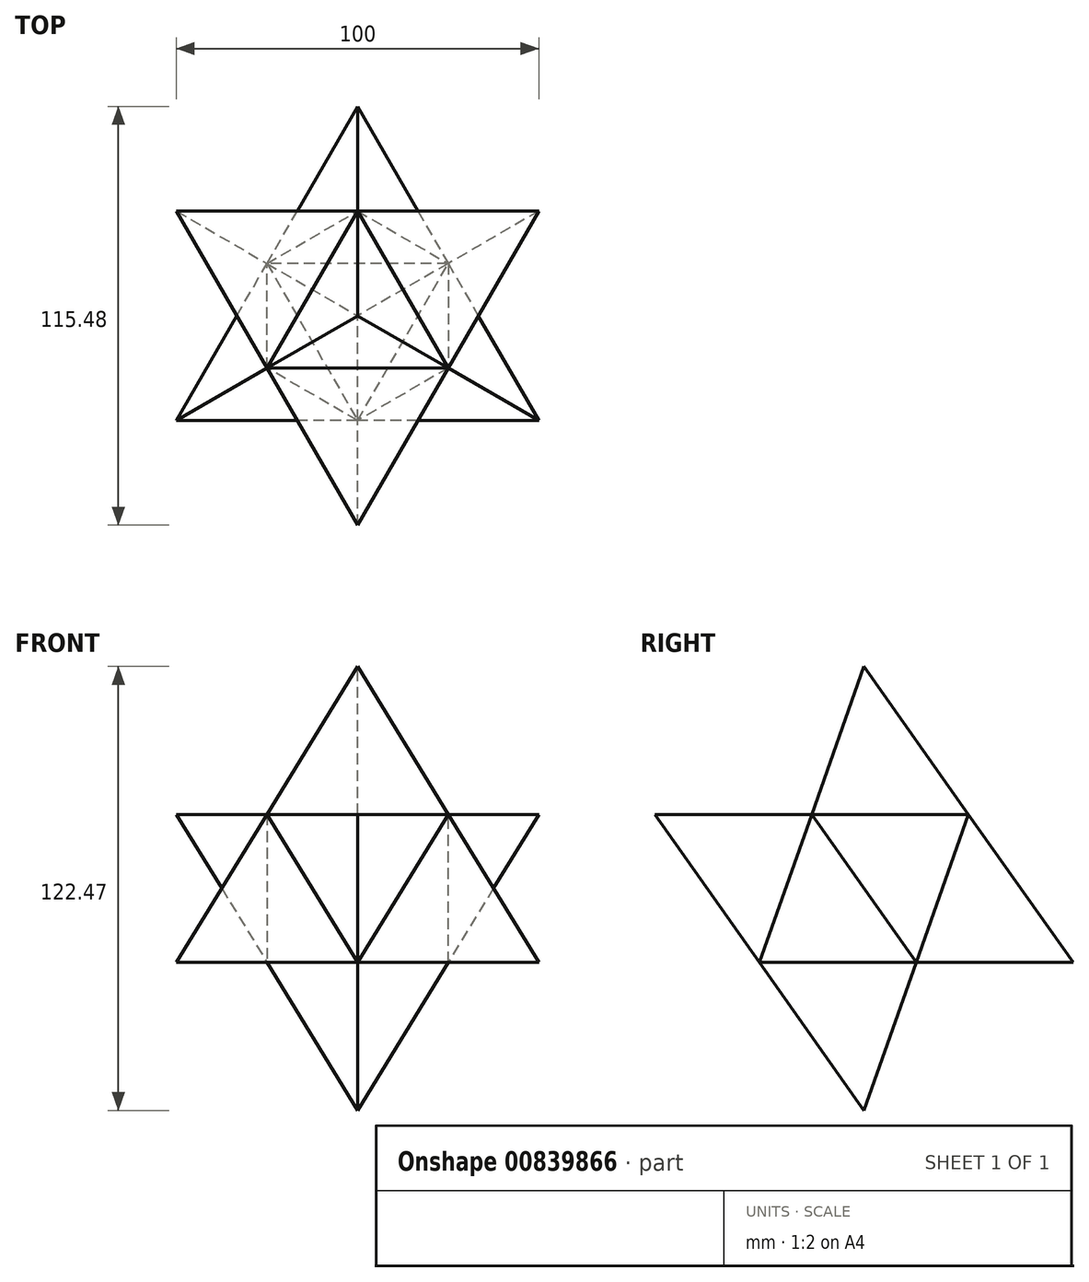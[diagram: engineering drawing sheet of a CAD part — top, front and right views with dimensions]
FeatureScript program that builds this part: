
annotation { "Feature Type Name" : "Feature", "Feature Type Description" : "" }
export const myFeature = defineFeature(function(context is Context, id is Id, definition is map)
    precondition{}
    {
        {
            var Q0;
            Q0=qCreatedBy(makeId("Top.planeOp"),FACE);
            var sketch = newSketch(context, id + "F0", { "sketchPlane" : qUnion([Q0])});
            skCircle(sketch, "E0.cCircle", {"center": v(0, 0) * mm, "radius": 28.87 * mm, "construction": true});
            skLineSegment(sketch, "E0.0", {"start": v(-50, -28.87) * mm, "end": v(0, 57.74) * mm});
            skLineSegment(sketch, "E0.1", {"start": v(0, 57.74) * mm, "end": v(50, -28.87) * mm});
            skLineSegment(sketch, "E0.2", {"start": v(50, -28.87) * mm, "end": v(-50, -28.87) * mm});
            skPoint(sketch, "E0.0.midPoint", {"position": v(-25, 14.43) * mm});
            skLineSegment(sketch, "E1", {"start": v(0, 57.74) * mm, "end": v(0, -28.87) * mm, "construction": true});
            skSolve(sketch);
        }
        {
            var Q0;
            Q0=qCreatedBy(makeId("Right.planeOp"),FACE);
            var sketch = newSketch(context, id + "F1", { "sketchPlane" : qUnion([Q0])});
            skLineSegment(sketch, "E2", {"start": v(0, 0) * mm, "end": v(0, 81.65) * mm, "construction": true});
            skLineSegment(sketch, "E3", {"start": v(0, 81.65) * mm, "end": v(-28.87, 0) * mm, "construction": true});
            skSolve(sketch);
        }
        {
            var Q0;
            Q0=makeQuery(id+"F0.imprint","IMPRINT",FACE,{"disambiguationData":[TD([[makeQuery(id+"F0.imprint","IMPRINT",EDGE,{"derivedFrom":sQuery(id+"F0.wireOp",EDGE,"E0.0")}),-1.0]])]});
            var Q1;
            Q1=sQuery(id+"F1.wireOp",VERTEX,"E2.end");
            loft(context, id + "F2", {"sheetProfilesArray" : [{ "sheetProfileEntities" : qUnion([Q0]) }, { "sheetProfileEntities" : qUnion([Q1]) }]});
        }
        {
            var Q0;
            {var subQ0=sQuery(id+"F0.wireOp",EDGE,"E0.2");var subQ1=sQuery(id+"F0.wireOp",EDGE,"E0.1");var subQ2=sQuery(id+"F0.wireOp",EDGE,"E0.0");Q0=makeQuery(id+"F2.opLoft","SWEPT_FACE",FACE,{"disambiguationData":[OSD([subQ2,subQ1,subQ0]),TDD([makeQuery(id+"F0.imprint","INTERSECT",VERTEX,{"derivedFrom":[subQ2,subQ0]}),makeQuery(id+"F0.imprint","INTERSECT",VERTEX,{"derivedFrom":[subQ1,subQ0]}),makeQuery(id+"F0.imprint","IMPRINT",EDGE,{"derivedFrom":subQ0})])]});}
            var sketch = newSketch(context, id + "F3", { "sketchPlane" : qUnion([Q0])});
            skLineSegment(sketch, "E4.0", {"start": v(41.34, -4.62) * mm, "end": v(0, 66.98) * mm});
            skLineSegment(sketch, "E4.1", {"start": v(-41.34, -4.62) * mm, "end": v(41.34, -4.62) * mm});
            skLineSegment(sketch, "E4.2", {"start": v(0, 66.98) * mm, "end": v(-41.34, -4.62) * mm});
            skSolve(sketch);
        }
        {
            var Q0;
            {var subQ0=sQuery(id+"F0.wireOp",EDGE,"E0.1");var subQ1=sQuery(id+"F0.wireOp",EDGE,"E0.2");var subQ2=sQuery(id+"F0.wireOp",EDGE,"E0.0");Q0=makeQuery(id+"F2.opLoft","SWEPT_FACE",FACE,{"disambiguationData":[OSD([subQ2,subQ0,subQ1]),TDD([makeQuery(id+"F0.imprint","INTERSECT",VERTEX,{"derivedFrom":[subQ2,subQ0]}),makeQuery(id+"F0.imprint","INTERSECT",VERTEX,{"derivedFrom":[subQ0,subQ1]}),makeQuery(id+"F0.imprint","IMPRINT",EDGE,{"derivedFrom":subQ0})])]});}
            var sketch = newSketch(context, id + "F4", { "sketchPlane" : qUnion([Q0])});
            skLineSegment(sketch, "E5.0", {"start": v(41.47, 3.27) * mm, "end": v(-12.66, 65.77) * mm});
            skLineSegment(sketch, "E5.1", {"start": v(-39.72, -12.35) * mm, "end": v(41.47, 3.27) * mm});
            skLineSegment(sketch, "E5.2", {"start": v(-12.66, 65.77) * mm, "end": v(-39.72, -12.35) * mm});
            skSolve(sketch);
        }
        {
            var Q0;
            {var subQ0=sQuery(id+"F0.wireOp",EDGE,"E0.0");var subQ1=sQuery(id+"F0.wireOp",EDGE,"E0.1");var subQ2=sQuery(id+"F0.wireOp",EDGE,"E0.2");Q0=makeQuery(id+"F2.opLoft","SWEPT_FACE",FACE,{"disambiguationData":[OSD([subQ0,subQ1,subQ2]),TDD([makeQuery(id+"F0.imprint","INTERSECT",VERTEX,{"derivedFrom":[subQ0,subQ2]}),makeQuery(id+"F0.imprint","INTERSECT",VERTEX,{"derivedFrom":[subQ0,subQ1]}),makeQuery(id+"F0.imprint","IMPRINT",EDGE,{"derivedFrom":subQ0})])]});}
            var sketch = newSketch(context, id + "F5", { "sketchPlane" : qUnion([Q0])});
            skLineSegment(sketch, "E6.0", {"start": v(39.72, -12.35) * mm, "end": v(12.66, 65.77) * mm});
            skLineSegment(sketch, "E6.1", {"start": v(-41.47, 3.27) * mm, "end": v(39.72, -12.35) * mm});
            skLineSegment(sketch, "E6.2", {"start": v(12.66, 65.77) * mm, "end": v(-41.47, 3.27) * mm});
            skSolve(sketch);
        }
        {
            var Q0;
            Q0=makeQuery(id+"F2.opLoft","CAP_FACE",FACE,{"disambiguationData":[OSD([makeQuery(id+"F0.imprint","IMPRINT",FACE,{"disambiguationData":[TD([[makeQuery(id+"F0.imprint","IMPRINT",EDGE,{"derivedFrom":sQuery(id+"F0.wireOp",EDGE,"E0.0")}),-1.0]])]})])],"isStart":true});
            var sketch = newSketch(context, id + "F6", { "sketchPlane" : qUnion([Q0])});
            skLineSegment(sketch, "E7.0", {"start": v(-41.34, 23.87) * mm, "end": v(41.34, 23.87) * mm});
            skLineSegment(sketch, "E7.1", {"start": v(0, -47.74) * mm, "end": v(-41.34, 23.87) * mm});
            skLineSegment(sketch, "E7.2", {"start": v(41.34, 23.87) * mm, "end": v(0, -47.74) * mm});
            skSolve(sketch);
        }
        {
            var Q0;
            Q0=makeQuery(id+"F2.opLoft","SWEPT_BODY",BODY,{"disambiguationData":[OSD([makeQuery(id+"F0.imprint","IMPRINT",FACE,{"disambiguationData":[TD([[makeQuery(id+"F0.imprint","IMPRINT",EDGE,{"derivedFrom":sQuery(id+"F0.wireOp",EDGE,"E0.0")}),-1.0]])]}),sQuery(id+"F1.wireOp",VERTEX,"E2.end")])]});
            var Q1;
            Q1=qCreatedBy(makeId("Top.planeOp"),FACE);
            mirror(context, id + "F7", {"entities" : qUnion([Q0]), "mirrorPlane" : qUnion([Q1])});
        }
        {
            var Q0;
            Q0=makeQuery(id+"F7.opPattern","COPY",BODY,{"derivedFrom":makeQuery(id+"F2.opLoft","SWEPT_BODY",BODY,{"disambiguationData":[OSD([makeQuery(id+"F0.imprint","IMPRINT",FACE,{"disambiguationData":[TD([[makeQuery(id+"F0.imprint","IMPRINT",EDGE,{"derivedFrom":sQuery(id+"F0.wireOp",EDGE,"E0.0")}),-1.0]])]}),sQuery(id+"F1.wireOp",VERTEX,"E2.end")])]}),"instanceName":"1"});
            var Q1;
            Q1=sQuery(id+"F1.wireOp",EDGE,"E2");
            transform(context, id + "F8", {"entities" : qUnion([Q0]), "transformType" : TransformType.ROTATION, "transformAxis" : qUnion([Q1]), "angle" : 60 * degree, "makeCopy" : false});
        }
        {
            var Q0;
            Q0=qCreatedBy(makeId("Front.planeOp"),FACE);
            var sketch = newSketch(context, id + "F9", { "sketchPlane" : qUnion([Q0])});
            skLineSegment(sketch, "E8", {"start": v(0, 0) * mm, "end": v(0, 40.82) * mm});
            skSolve(sketch);
        }
        {
            var Q0;
            Q0=makeQuery(id+"F7.opPattern","COPY",BODY,{"derivedFrom":makeQuery(id+"F2.opLoft","SWEPT_BODY",BODY,{"disambiguationData":[OSD([makeQuery(id+"F0.imprint","IMPRINT",FACE,{"disambiguationData":[TD([[makeQuery(id+"F0.imprint","IMPRINT",EDGE,{"derivedFrom":sQuery(id+"F0.wireOp",EDGE,"E0.0")}),-1.0]])]}),sQuery(id+"F1.wireOp",VERTEX,"E2.end")])]}),"instanceName":"1"});
            var Q1;
            Q1=sQuery(id+"F9.wireOp",EDGE,"E8");
            transform(context, id + "F10", {"entities" : qUnion([Q0]), "transformType" : TransformType.TRANSLATION_ENTITY, "oppositeDirectionEntity" : false, "transformLine" : qUnion([Q1]), "makeCopy" : false});
        }
        {
            var Q0;
            Q0=makeQuery(id+"F7.opPattern","COPY",BODY,{"derivedFrom":makeQuery(id+"F2.opLoft","SWEPT_BODY",BODY,{"disambiguationData":[OSD([makeQuery(id+"F0.imprint","IMPRINT",FACE,{"disambiguationData":[TD([[makeQuery(id+"F0.imprint","IMPRINT",EDGE,{"derivedFrom":sQuery(id+"F0.wireOp",EDGE,"E0.0")}),-1.0]])]}),sQuery(id+"F1.wireOp",VERTEX,"E2.end")])]}),"instanceName":"1"});
            var Q1;
            Q1=makeQuery(id+"F2.opLoft","SWEPT_BODY",BODY,{"disambiguationData":[OSD([makeQuery(id+"F0.imprint","IMPRINT",FACE,{"disambiguationData":[TD([[makeQuery(id+"F0.imprint","IMPRINT",EDGE,{"derivedFrom":sQuery(id+"F0.wireOp",EDGE,"E0.0")}),-1.0]])]}),sQuery(id+"F1.wireOp",VERTEX,"E2.end")])]});
            booleanBodies(context, id + "F11", {"operationType" : BooleanOperationType.UNION, "tools" : qUnion([Q0, Q1])});
        }
    });
